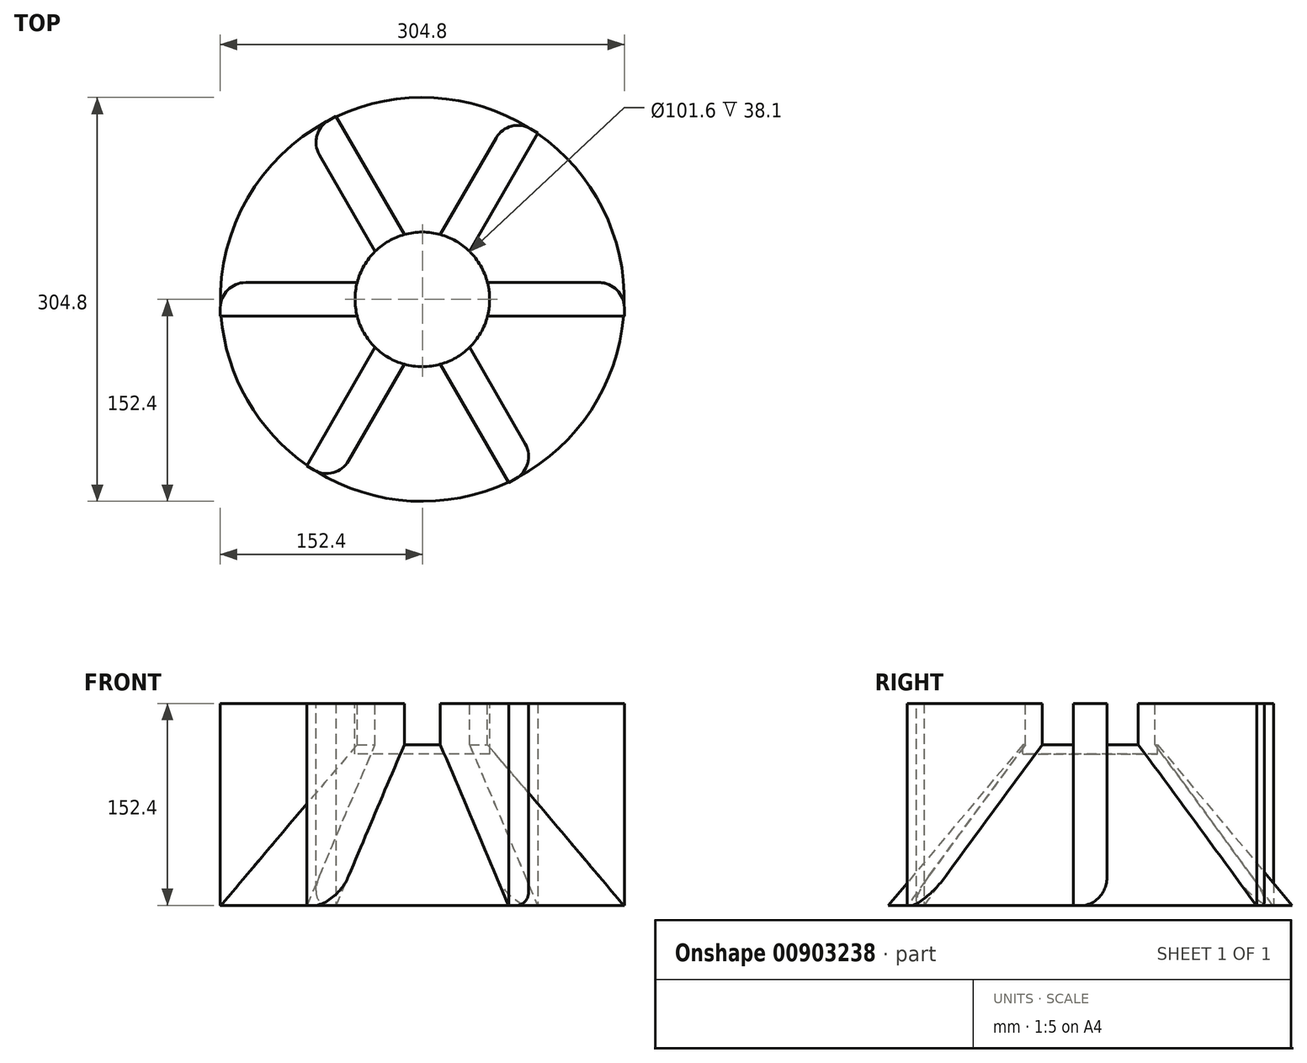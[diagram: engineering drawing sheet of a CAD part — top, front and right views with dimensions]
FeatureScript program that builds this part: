
annotation { "Feature Type Name" : "Feature", "Feature Type Description" : "" }
export const myFeature = defineFeature(function(context is Context, id is Id, definition is map)
    precondition{}
    {
        {
            var Q0;
            Q0=qCreatedBy(makeId("Top.planeOp"),FACE);
            var sketch = newSketch(context, id + "F0", { "sketchPlane" : qUnion([Q0])});
            skCircle(sketch, "E0", {"center": v(0, 0) * mm, "radius": 152.4 * mm});
            skSolve(sketch);
        }
        {
            var Q0;
            Q0 = qSketchRegion(id + "F0", true);
            extrude(context, id + "F1", {"entities" : qUnion([Q0]), "depth" : 152.4 * mm, "offsetDistance" : 25.4 * mm, "hasDraft" : true, "draftAngle" : 40 * degree, "draftPullDirection" : true});
        }
        {
            var Q0;
            Q0=makeQuery(id+"F1.opExtrude","CAP_FACE",FACE,{"disambiguationData":[OSD([sQuery(id+"F0.wireOp",EDGE,"E0")])],"isStart":true});
            var sketch = newSketch(context, id + "F2", { "sketchPlane" : qUnion([Q0])});
            skLineSegment(sketch, "E1.bottom", {"start": v(152.4, -12.7) * mm, "end": v(-152.4, -12.7) * mm});
            skLineSegment(sketch, "E1.top", {"start": v(152.4, 12.7) * mm, "end": v(-152.4, 12.7) * mm});
            skLineSegment(sketch, "E1.left", {"start": v(152.4, -12.7) * mm, "end": v(152.4, 12.7) * mm});
            skLineSegment(sketch, "E1.right", {"start": v(-152.4, -12.7) * mm, "end": v(-152.4, 12.7) * mm});
            skPoint(sketch, "E1.middle", {"position": v(0, 0) * mm});
            skLineSegment(sketch, "E2.1.0", {"start": v(-65.2, 138.33) * mm, "end": v(87.2, -125.63) * mm});
            skLineSegment(sketch, "E2.1.1", {"start": v(-87.2, 125.63) * mm, "end": v(65.2, -138.33) * mm});
            skLineSegment(sketch, "E2.2.0", {"start": v(-87.2, -125.63) * mm, "end": v(65.2, 138.33) * mm});
            skLineSegment(sketch, "E2.2.1", {"start": v(-65.2, -138.33) * mm, "end": v(87.2, 125.63) * mm});
            skLineSegment(sketch, "E3.1.0", {"start": v(87.2, -125.63) * mm, "end": v(65.2, -138.33) * mm});
            skLineSegment(sketch, "E3.2.0", {"start": v(65.2, 138.33) * mm, "end": v(87.2, 125.63) * mm});
            skLineSegment(sketch, "E4.1.0", {"start": v(-65.2, 138.33) * mm, "end": v(-87.2, 125.63) * mm});
            skLineSegment(sketch, "E4.2.0", {"start": v(-87.2, -125.63) * mm, "end": v(-65.2, -138.33) * mm});
            skSolve(sketch);
        }
        {
            var Q0;
            Q0 = qSketchRegion(id + "F2", true);
            extrude(context, id + "F3", {"entities" : qUnion([Q0]), "operationType" : NewBodyOperationType.ADD, "oppositeDirection" : true, "depth" : 152.4 * mm, "offsetDistance" : 25.4 * mm});
        }
        {
            var Q0;
            Q0=makeQuery(id+"F3.boolean.opBoolean","MERGE",FACE,{"derivedFrom":[makeQuery(id+"F1.opExtrude","CAP_FACE",FACE,{"disambiguationData":[OSD([sQuery(id+"F0.wireOp",EDGE,"E0")])],"isStart":false}),makeQuery(id+"F3.opExtrude","CAP_FACE",FACE,{"disambiguationData":[OSD([sQuery(id+"F2.wireOp",EDGE,"E1.bottom"),sQuery(id+"F2.wireOp",EDGE,"E1.top"),sQuery(id+"F2.wireOp",EDGE,"E1.left"),sQuery(id+"F2.wireOp",EDGE,"E1.right"),sQuery(id+"F2.wireOp",EDGE,"E2.1.0"),sQuery(id+"F2.wireOp",EDGE,"E2.1.1"),sQuery(id+"F2.wireOp",EDGE,"E2.2.0"),sQuery(id+"F2.wireOp",EDGE,"E2.2.1"),sQuery(id+"F2.wireOp",EDGE,"E3.1.0"),sQuery(id+"F2.wireOp",EDGE,"E3.2.0"),sQuery(id+"F2.wireOp",EDGE,"E4.1.0"),sQuery(id+"F2.wireOp",EDGE,"E4.2.0")])],"isStart":false})]});
            var sketch = newSketch(context, id + "F4", { "sketchPlane" : qUnion([Q0])});
            skCircle(sketch, "E5", {"center": v(0, 0) * mm, "radius": 50.8 * mm});
            skSolve(sketch);
        }
        {
            var Q0;
            Q0 = qSketchRegion(id + "F4", true);
            extrude(context, id + "F5", {"entities" : qUnion([Q0]), "operationType" : NewBodyOperationType.REMOVE, "oppositeDirection" : true, "depth" : 38.1 * mm, "offsetDistance" : 25.4 * mm});
        }
        {
            var Q0;
            Q0=makeQuery(id+"F3.opExtrude","SWEPT_EDGE",EDGE,{"disambiguationData":[OSD([sQuery(id+"F2.wireOp",EDGE,"E2.2.1"),sQuery(id+"F2.wireOp",EDGE,"E3.2.0")])]});
            var Q1;
            Q1=makeQuery(id+"F3.opExtrude","SWEPT_EDGE",EDGE,{"disambiguationData":[OSD([sQuery(id+"F2.wireOp",EDGE,"E2.1.0"),sQuery(id+"F2.wireOp",EDGE,"E4.1.0")])]});
            var Q2;
            Q2=makeQuery(id+"F3.opExtrude","SWEPT_EDGE",EDGE,{"disambiguationData":[OSD([sQuery(id+"F2.wireOp",EDGE,"E1.bottom"),sQuery(id+"F2.wireOp",EDGE,"E1.left")])]});
            var Q3;
            Q3=makeQuery(id+"F3.opExtrude","SWEPT_EDGE",EDGE,{"disambiguationData":[OSD([sQuery(id+"F2.wireOp",EDGE,"E2.1.1"),sQuery(id+"F2.wireOp",EDGE,"E3.1.0")])]});
            var Q4;
            Q4=makeQuery(id+"F3.opExtrude","SWEPT_EDGE",EDGE,{"disambiguationData":[OSD([sQuery(id+"F2.wireOp",EDGE,"E2.2.0"),sQuery(id+"F2.wireOp",EDGE,"E4.2.0")])]});
            var Q5;
            Q5=makeQuery(id+"F3.opExtrude","SWEPT_EDGE",EDGE,{"disambiguationData":[OSD([sQuery(id+"F2.wireOp",EDGE,"E1.bottom"),sQuery(id+"F2.wireOp",EDGE,"E1.right")])]});
            fillet(context, id + "F6", {"entities" : qUnion([Q0, Q1, Q2, Q3, Q4, Q5]), "radius" : 19.05 * mm, "tangentPropagation" : true, "allowEdgeOverflow" : false});
        }
    });
